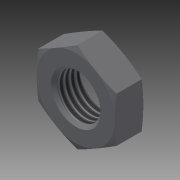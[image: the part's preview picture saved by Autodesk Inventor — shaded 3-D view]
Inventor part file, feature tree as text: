
AUTODESK INVENTOR PART (.ipt)
format: ipt  version: 2013 (Build 170138000, 138)  size: 154,112 bytes
history: native  units: in
note: dims shown in document units (in); Inventor stores cm internally (conversion verified against a paired STEP export)
features: other x70, sketch x3, revolve x2, extrude x1, thread x1
ambient origin geometry x8: Origin, YZ Plane, XZ Plane, XY Plane, X Axis, Y Axis, Z Axis, Center Point
bodies: Solid1 (feature_tree)
feature tree (77):
  sketch  "Sketch_8"  dims[d0=360.0deg d1=0.25in d2=0.0in]
  sketch  "Sketch_10"  dims[d3=360.0deg d4=0.1959in d5=0.0in]
  revolve  "Revolution1"  [1 undecoded]
  extrude  "Extrusion1"  Depth=0.1959in TaperAngle=0.0deg
  revolve  "Revolution2"  [1 undecoded]
  thread  "Thread1"  [1 undecoded]
  other  "NUT_XY"
  other  "NUT_YZ"
  other  "NUT_ZX"
  other  "NUT_X"
  other  "NUT_Y"
  other  "NUT_Z"
  other  "NUT_Center"
  other  "a1_XY"
  other  "a1_YZ"
  other  "a1_ZX"
  other  "a1_X"
  other  "a1_Y"
  other  "a1_Z"
  other  "a1_Center"
  other  "a2_XY"
  other  "a2_YZ"
  other  "a2_ZX"
  other  "a2_X"
  other  "a2_Y"
  other  "a2_Z"
  other  "a2_Center"
  other  "b1_XY"
  other  "b1_YZ"
  other  "b1_ZX"
  other  "b1_X"
  other  "b1_Y"
  other  "b1_Z"
  other  "b1_Center"
  other  "b2_XY"
  other  "b2_YZ"
  other  "b2_ZX"
  other  "b2_X"
  other  "b2_Y"
  other  "b2_Z"
  other  "b2_Center"
  other  "e_XY"
  other  "e_YZ"
  other  "e_ZX"
  other  "e_X"
  other  "e_Y"
  other  "e_Z"
  other  "e_Center"
  other  "th1_XY"
  other  "th1_YZ"
  other  "th1_ZX"
  other  "th1_X"
  other  "th1_Y"
  other  "th1_Z"
  other  "th1_Center"
  other  "th2_XY"
  other  "th2_YZ"
  other  "th2_ZX"
  other  "th2_X"
  other  "th2_Y"
  other  "th2_Z"
  other  "th2_Center"
  other  "ol1_XY"
  other  "ol1_YZ"
  other  "ol1_ZX"
  other  "ol1_X"
  other  "ol1_Y"
  other  "ol1_Z"
  other  "ol1_Center"
  other  "ol2_XY"
  other  "ol2_YZ"
  other  "ol2_ZX"
  other  "ol2_X"
  other  "ol2_Y"
  other  "ol2_Z"
  other  "ol2_Center"
  sketch  "Sketch_11"
note: 3 required parameter values undecoded (feature->parameter linkage not recoverable at this tier; creation-order binding heuristic only, values carry confidence <= 0.55)